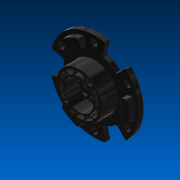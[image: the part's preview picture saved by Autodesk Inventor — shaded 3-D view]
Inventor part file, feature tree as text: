
AUTODESK INVENTOR PART (.ipt)
format: ipt  version: 2022.2 (Build 262287000, 287)  size: 925,696 bytes
history: native  units: in
note: dims shown in document units (in); Inventor stores cm internally (conversion verified against a paired STEP export)
features: fillet x1
ambient origin geometry x8: Origin, YZ Plane, XZ Plane, XY Plane, X Axis, Y Axis, Z Axis, Center Point
bodies: Solid1 (feature_tree)
feature tree (1):
  fillet  "Fillet27"  [1 undecoded]
note: 1 required parameter value undecoded (feature->parameter linkage not recoverable at this tier; creation-order binding heuristic only, values carry confidence <= 0.55)
